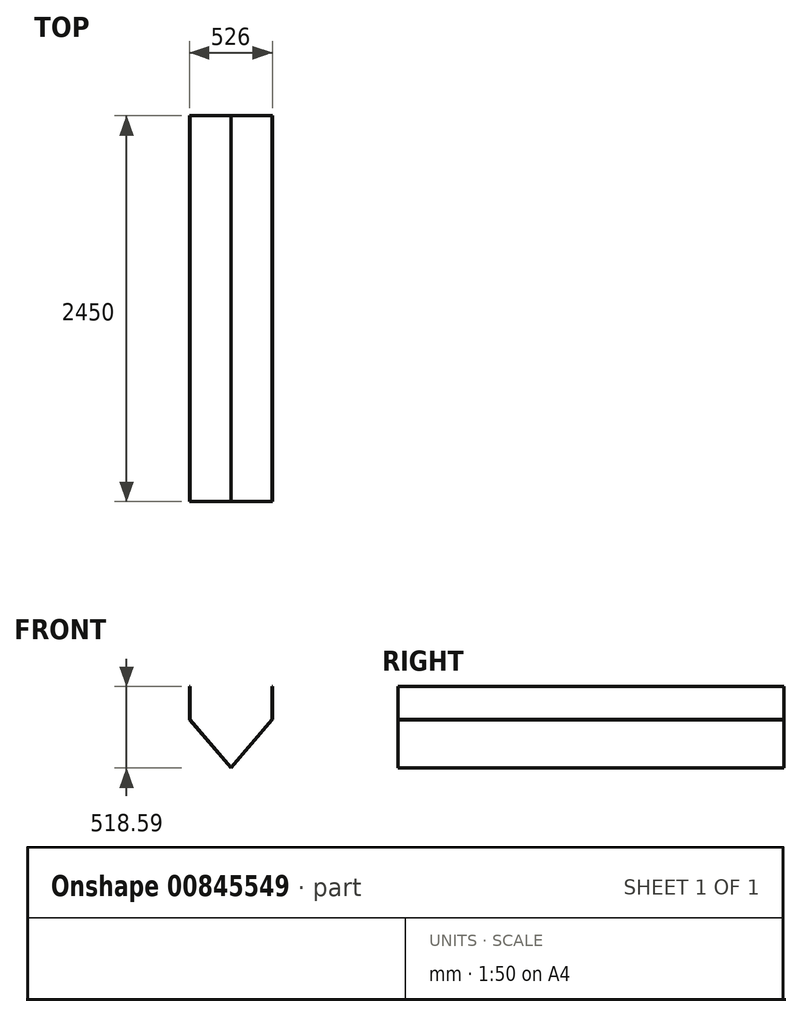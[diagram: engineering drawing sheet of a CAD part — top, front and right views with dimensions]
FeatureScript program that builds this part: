
annotation { "Feature Type Name" : "Feature", "Feature Type Description" : "" }
export const myFeature = defineFeature(function(context is Context, id is Id, definition is map)
    precondition{}
    {
        {
            var Q0;
            Q0=qCreatedBy(makeId("Front.planeOp"),FACE);
            var sketch = newSketch(context, id + "F0", { "sketchPlane" : qUnion([Q0])});
            skLineSegment(sketch, "E0", {"start": v(-50.33, 224.51) * mm, "end": v(-50.33, 14.51) * mm});
            skLineSegment(sketch, "E1", {"start": v(-50.33, 14.51) * mm, "end": v(209.67, -289.46) * mm});
            skLineSegment(sketch, "E2", {"start": v(209.67, -289.46) * mm, "end": v(469.67, 14.51) * mm});
            skLineSegment(sketch, "E3", {"start": v(469.67, 14.51) * mm, "end": v(469.67, 224.51) * mm});
            skLineSegment(sketch, "E4.0", {"start": v(-53.33, 224.51) * mm, "end": v(-53.33, 14.51) * mm});
            skLineSegment(sketch, "E5.0", {"start": v(-52.6, 12.56) * mm, "end": v(207.4, -291.4) * mm});
            skLineSegment(sketch, "E6.0", {"start": v(211.95, -291.4) * mm, "end": v(471.95, 12.56) * mm});
            skLineSegment(sketch, "E7.0", {"start": v(472.67, 14.51) * mm, "end": v(472.67, 224.51) * mm});
            skLineSegment(sketch, "E8", {"start": v(-50.33, 224.51) * mm, "end": v(-53.33, 224.51) * mm});
            skLineSegment(sketch, "E9", {"start": v(469.67, 224.51) * mm, "end": v(472.67, 224.51) * mm});
            skLineSegment(sketch, "E10", {"start": v(207.4, -291.4) * mm, "end": v(209.67, -294.08) * mm});
            skLineSegment(sketch, "E11", {"start": v(209.67, -294.08) * mm, "end": v(211.95, -291.4) * mm});
            skLineSegment(sketch, "E12", {"start": v(-53.33, 14.51) * mm, "end": v(-52.6, 12.56) * mm});
            skLineSegment(sketch, "E13", {"start": v(471.95, 12.56) * mm, "end": v(472.67, 14.51) * mm});
            skSolve(sketch);
        }
        {
            var Q0;
            Q0=makeQuery(id+"F0.imprint","IMPRINT",FACE,{"disambiguationData":[TD([[makeQuery(id+"F0.imprint","IMPRINT",EDGE,{"derivedFrom":sQuery(id+"F0.wireOp",EDGE,"E0")}),-1.0]])]});
            extrude(context, id + "F1", {"entities" : qUnion([Q0]), "depth" : 2450 * mm, "offsetDistance" : 25 * mm});
        }
    });
